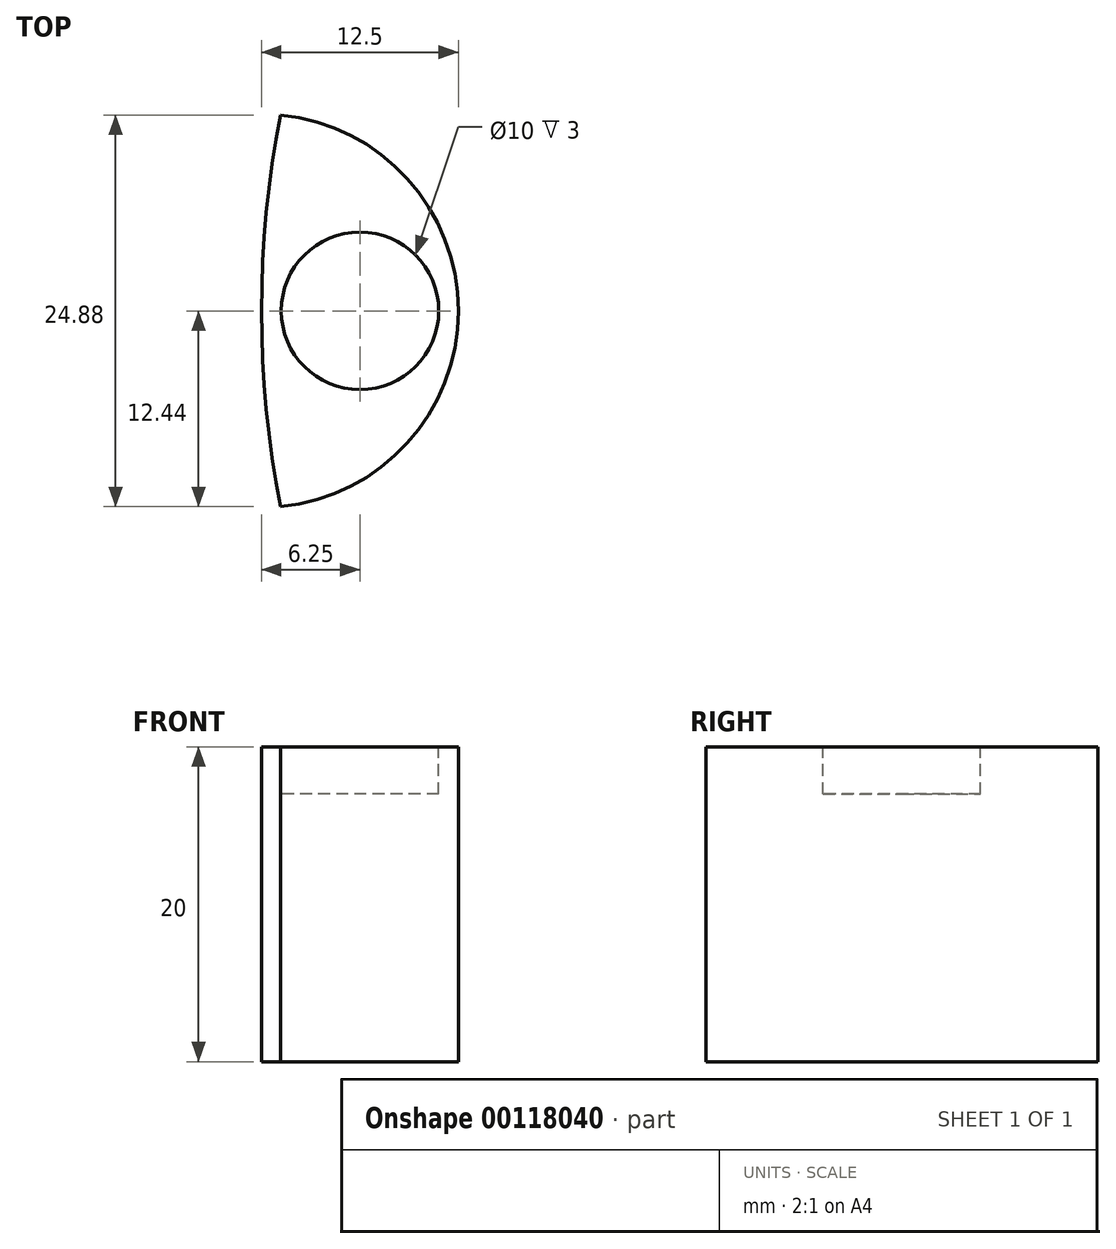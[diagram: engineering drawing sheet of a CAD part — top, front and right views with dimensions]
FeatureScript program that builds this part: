
annotation { "Feature Type Name" : "Feature", "Feature Type Description" : "" }
export const myFeature = defineFeature(function(context is Context, id is Id, definition is map)
    precondition{}
    {
        {
            var Q0;
            Q0=qCreatedBy(makeId("Top.planeOp"),FACE);
            var sketch = newSketch(context, id + "F0", { "sketchPlane" : qUnion([Q0])});
            skArc(sketch, "E0", {"start": v(-63.8, 12.44) * mm, "mid": v(-65, 0) * mm, "end": v(-63.8, -12.44) * mm});
            skArc(sketch, "E1", {"start": v(-63.8, -12.44) * mm, "mid": v(-52.5, 0) * mm, "end": v(-63.8, 12.44) * mm});
            skSolve(sketch);
        }
        {
            var Q0;
            Q0=qSketchRegion(id+"F0",true);
            extrude(context, id + "F1", {"entities" : qUnion([Q0]), "depth" : 20 * mm});
        }
        {
            var Q0;
            Q0=makeQuery(id+"F1.opExtrude","CAP_FACE",FACE,{"disambiguationData":[OSD([sQuery(id+"F0.wireOp",EDGE,"E0"),sQuery(id+"F0.wireOp",EDGE,"E1")])],"isStart":false});
            var sketch = newSketch(context, id + "F2", { "sketchPlane" : qUnion([Q0])});
            skLineSegment(sketch, "E2", {"start": v(-65, 0) * mm, "end": v(-52.5, 0) * mm});
            skCircle(sketch, "E3", {"center": v(-58.75, 0) * mm, "radius": 5 * mm});
            skSolve(sketch);
        }
        {
            var Q0;
            {var subQ0=sQuery(id+"F2.wireOp",EDGE,"E3");var subQ1=sQuery(id+"F2.wireOp",EDGE,"E2");var subQ2=makeQuery(id+"F2.imprint","INTERSECT",VERTEX,{"disambiguationData":[OD(0.0)],"derivedFrom":[subQ1,subQ0]});Q0=makeQuery(id+"F2.imprint","IMPRINT",FACE,{"disambiguationData":[TD([[makeQuery(id+"F2.imprint","IMPRINT",EDGE,{"disambiguationData":[TD([[subQ2,-1.0]])],"derivedFrom":subQ1}),-1.0]])]});}
            var Q1;
            {var subQ0=sQuery(id+"F2.wireOp",EDGE,"E3");var subQ1=sQuery(id+"F2.wireOp",EDGE,"E2");var subQ2=makeQuery(id+"F2.imprint","INTERSECT",VERTEX,{"disambiguationData":[OD(0.0)],"derivedFrom":[subQ1,subQ0]});Q1=makeQuery(id+"F2.imprint","IMPRINT",FACE,{"disambiguationData":[TD([[makeQuery(id+"F2.imprint","IMPRINT",EDGE,{"disambiguationData":[TD([[subQ2,-1.0]])],"derivedFrom":subQ1}),1.0]])]});}
            extrude(context, id + "F3", {"entities" : qUnion([Q0, Q1]), "operationType" : NewBodyOperationType.REMOVE, "oppositeDirection" : true, "depth" : 3 * mm});
        }
    });
